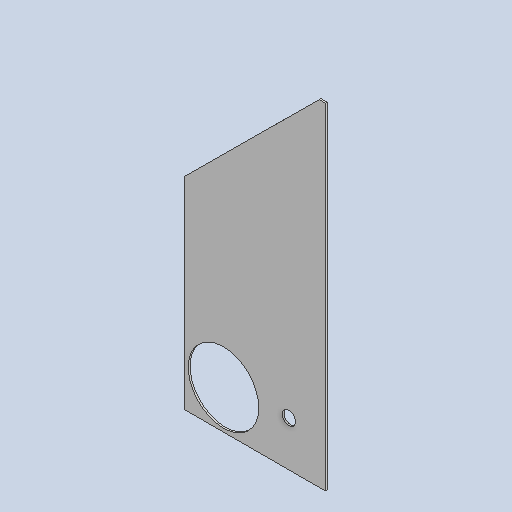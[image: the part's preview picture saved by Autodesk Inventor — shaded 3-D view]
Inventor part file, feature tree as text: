
AUTODESK INVENTOR PART (.ipt)
format: ipt  version: 2025 (Build 290162010, 162A)  size: 178,176 bytes
history: native  units: mm
features: extrude x3, sketch x2, projected_geometry x1, other x1
ambient origin geometry x8: Origin, YZ Plane, XZ Plane, XY Plane, X Axis, Y Axis, Z Axis, Center Point
bodies: Solid1 (feature_tree)
feature tree (7):
  extrude  "Extrusion1"  Depth=1150.0mm
  extrude  "Extrusion3"  Depth=1180.0mm
  extrude  "Extrusion4"  Depth=10.0mm
  sketch  "Sketch3"  dims[d1=840.0mm d3=1150.0mm]
  sketch  "Sketch4"  dims[d11=390.0mm d12=1180.0mm d13=950.0mm d14=76.0mm d15=1910.0mm d16=255.0mm d17=220.0mm d18=401.0mm d19=220.0mm d21=1277.0mm d22=1554.635823mm d23=100.0mm d24=10.0mm d25=0.0mm d33=2140.0mm d34=494.0mm d37=10.0mm d38=0.0mm d45=310.0mm d47=5.0mm d48=80.0mm d49=372.0mm d51=780.0mm d52=1078.0mm d53=1340.0mm d54=0.0mm d55=0.0mm]
  projected_geometry  "Projected Loop1"
  other  "Definition1"
